# Revit family: QSC TSC-50-G3
name_source: partatom
category: Communication Devices
revit_build: Autodesk Revit 2018 (Build: 20190510_1515(x64)
units: mm (PartAtom-declared; Revit-internal decimal feet)

## family parameters
Cut with Voids When Loaded = Yes
Host = Face
Maintain Annotation Orientation = No
Part Type = Normal
Room Calculation Point = No
Round Connector Dimension = Use Diameter
Shared = No

## types (1)
- QSC TSC-50-G3
    Communication Ports = 1 Gbps RJ45 LAN
    Default Elevation = 0.0 mm
    Depth = 37.8 mm
    Description = PoE Touch Screen Controller
    Enclosure Material = Steel, Paint Finish, Dark Gray, Matte
    Face Material = Glossy Black
    Heat Load Active = 18
    Height = 81.3 mm
    Manufacturer = QSC, LLC
    Manufacturer URL = http://www.qsc.com
    Model = TSC-50-G3
    Product Documentation Link = https://www.qsc.com
    Product Page URL = https://www.qsc.com
    Regulatory Compliance = UL, CAN ICES-3 (B)/NMB-3 (B)
    Screen Material = Metal Panel
    Temperature Max = 50° C
    Temperature Min = 0° C
    URL = https://www.qsc.com
    Voltage DC = PoE Class 2
    Weight Product (kg) = 0.249
    Weight Product (lb) = 0.55
    Width = 141.0 mm

## geometry (parser evidence)
native form markers: Blend x1, Sweep x2
no freeform markers — native parametric forms only
